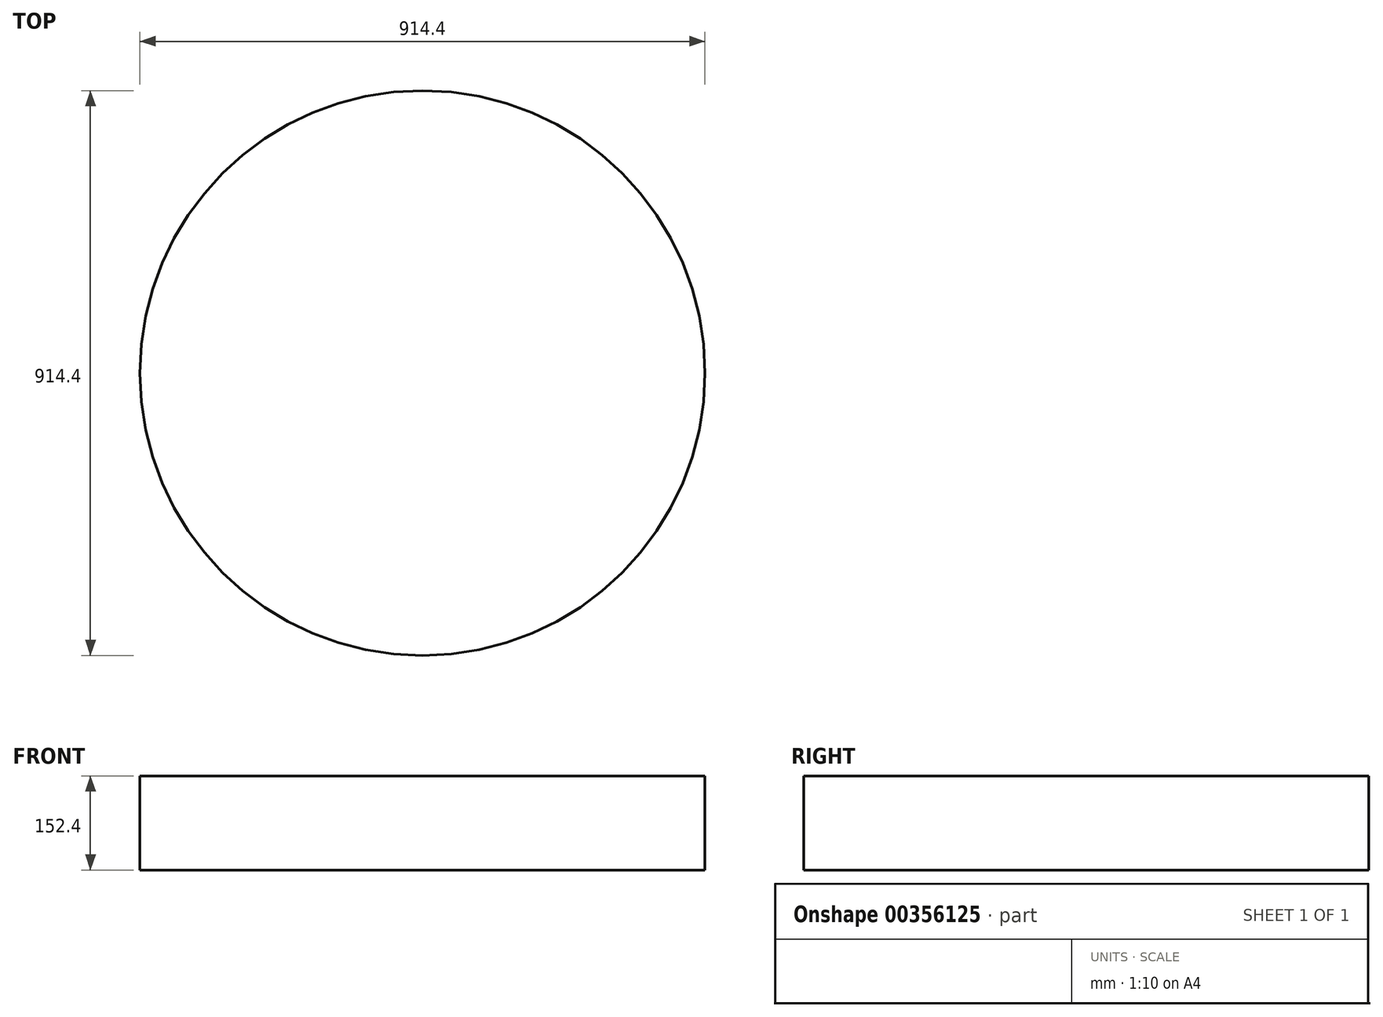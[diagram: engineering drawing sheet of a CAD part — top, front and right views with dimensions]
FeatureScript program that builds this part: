
annotation { "Feature Type Name" : "Feature", "Feature Type Description" : "" }
export const myFeature = defineFeature(function(context is Context, id is Id, definition is map)
    precondition{}
    {
        {
            var Q0;
            Q0=qCreatedBy(makeId("Top.planeOp"),FACE);
            var sketch = newSketch(context, id + "F0", { "sketchPlane" : qUnion([Q0])});
            skCircle(sketch, "E0", {"center": v(0, 0) * mm, "radius": 457.2 * mm});
            skSolve(sketch);
        }
        {
            var Q0;
            Q0=makeQuery(id+"F0.imprint","IMPRINT",FACE,{"disambiguationData":[TD([[makeQuery(id+"F0.imprint","IMPRINT",EDGE,{"derivedFrom":sQuery(id+"F0.wireOp",EDGE,"E0")}),1.0]])]});
            extrude(context, id + "F1", {"entities" : qUnion([Q0]), "depth" : 152.4 * mm});
        }
    });
